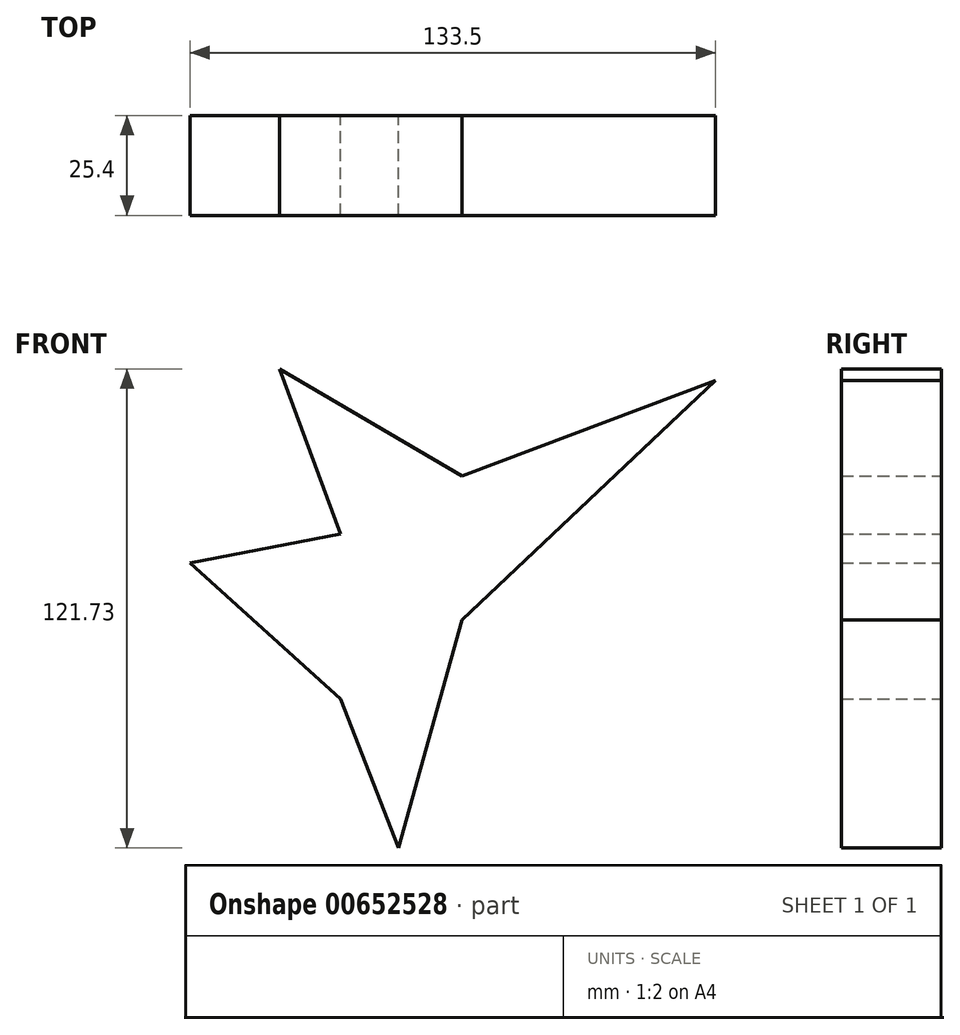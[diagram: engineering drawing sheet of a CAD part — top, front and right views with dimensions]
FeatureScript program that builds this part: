
annotation { "Feature Type Name" : "Feature", "Feature Type Description" : "" }
export const myFeature = defineFeature(function(context is Context, id is Id, definition is map)
    precondition{}
    {
        {
            var Q0;
            Q0=qCreatedBy(makeId("Front.planeOp"),FACE);
            var sketch = newSketch(context, id + "F0", { "sketchPlane" : qUnion([Q0])});
            skLineSegment(sketch, "E0", {"start": v(0, 0) * mm, "end": v(64.36, 60.87) * mm});
            skLineSegment(sketch, "E1", {"start": v(64.36, 60.87) * mm, "end": v(0, 36.6) * mm});
            skLineSegment(sketch, "E2", {"start": v(0, 36.6) * mm, "end": v(-46.34, 63.8) * mm});
            skLineSegment(sketch, "E3", {"start": v(-46.34, 63.8) * mm, "end": v(-30.9, 21.88) * mm});
            skLineSegment(sketch, "E4", {"start": v(-30.9, 21.88) * mm, "end": v(-69.14, 14.53) * mm});
            skLineSegment(sketch, "E5", {"start": v(-69.14, 14.53) * mm, "end": v(-30.9, -20.04) * mm});
            skLineSegment(sketch, "E6", {"start": v(-30.9, -20.04) * mm, "end": v(-16.18, -57.92) * mm});
            skLineSegment(sketch, "E7", {"start": v(-16.18, -57.92) * mm, "end": v(0, 0) * mm});
            skSolve(sketch);
        }
        {
            var Q0;
            Q0=makeQuery(id+"F0.imprint","IMPRINT",FACE,{"disambiguationData":[TD([[makeQuery(id+"F0.imprint","IMPRINT",EDGE,{"derivedFrom":sQuery(id+"F0.wireOp",EDGE,"E0")}),1.0]])]});
            extrude(context, id + "F1", {"entities" : qUnion([Q0]), "depth" : 25.4 * mm, "offsetDistance" : 25.4 * mm});
        }
    });
